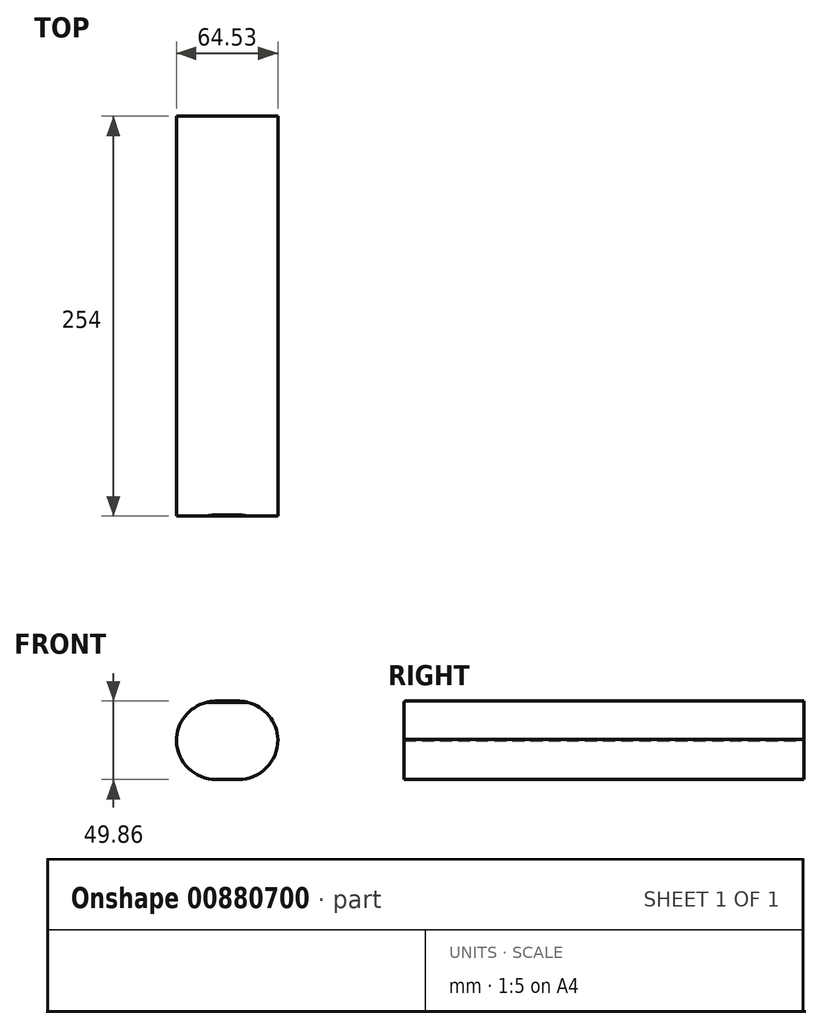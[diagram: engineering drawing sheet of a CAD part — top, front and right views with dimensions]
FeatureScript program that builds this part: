
annotation { "Feature Type Name" : "Feature", "Feature Type Description" : "" }
export const myFeature = defineFeature(function(context is Context, id is Id, definition is map)
    precondition{}
    {
        {
            var Q0;
            Q0=qCreatedBy(makeId("Front.planeOp"),FACE);
            var sketch = newSketch(context, id + "F0", { "sketchPlane" : qUnion([Q0])});
            skLineSegment(sketch, "E0.bottom", {"start": v(-64.53, 49.86) * mm, "end": v(0, 49.86) * mm});
            skLineSegment(sketch, "E0.top", {"start": v(-64.53, 0) * mm, "end": v(0, 0) * mm});
            skLineSegment(sketch, "E0.left", {"start": v(-64.53, 49.86) * mm, "end": v(-64.53, 0) * mm});
            skLineSegment(sketch, "E0.right", {"start": v(0, 49.86) * mm, "end": v(0, 0) * mm});
            skSolve(sketch);
        }
        {
            var Q0;
            Q0 = qSketchRegion(id + "F0", true);
            extrude(context, id + "F1", {"entities" : qUnion([Q0]), "depth" : 127 * mm, "offsetDistance" : 25.4 * mm, "hasSecondDirection" : true, "secondDirectionOppositeDirection" : true, "secondDirectionDepth" : 127 * mm});
        }
        {
            var Q0;
            Q0=makeQuery(id+"F1.opExtrude","CAP_FACE",FACE,{"disambiguationData":[OSD([sQuery(id+"F0.wireOp",EDGE,"E0.bottom"),sQuery(id+"F0.wireOp",EDGE,"E0.top"),sQuery(id+"F0.wireOp",EDGE,"E0.left"),sQuery(id+"F0.wireOp",EDGE,"E0.right")])],"isStart":false});
            var sketch = newSketch(context, id + "F2", { "sketchPlane" : qUnion([Q0])});
            skCircle(sketch, "E1", {"center": v(-34.08, 24.93) * mm, "radius": 15.41 * mm});
            skPoint(sketch, "E1.centerSnap0", {"position": v(-64.53, 24.93) * mm});
            skSolve(sketch);
        }
        {
            var Q0;
            Q0=makeQuery(id+"F1.opExtrude","CAP_EDGE",EDGE,{"disambiguationData":[OSD([sQuery(id+"F0.wireOp",EDGE,"E0.bottom")])],"isStart":false});
            chamfer(context, id + "F3", {"entities" : qUnion([Q0]), "width" : 0.76 * mm, "tangentPropagation" : true});
        }
        {
            var Q0;
            Q0=makeQuery(id+"F1.opExtrude","SWEPT_EDGE",EDGE,{"disambiguationData":[OSD([sQuery(id+"F0.wireOp",EDGE,"E0.bottom"),sQuery(id+"F0.wireOp",EDGE,"E0.left")])]});
            var Q1;
            {var subQ0=sQuery(id+"F0.wireOp",EDGE,"E0.right");Q1=makeQuery(id+"F9umjA94MgGjPcI_1.opFillet","BLEND_EDGE",EDGE,{"blendedFrom":[makeQuery(id+"F1.opExtrude","SWEPT_EDGE",EDGE,{"disambiguationData":[OSD([sQuery(id+"F0.wireOp",EDGE,"E0.bottom"),subQ0])]}),makeQuery(id+"F1.opExtrude","SWEPT_FACE",FACE,{"disambiguationData":[OSD([subQ0])]})],"blendedInto":[makeQuery(id+"F1.opExtrude","SWEPT_FACE",FACE,{"disambiguationData":[OSD([subQ0])]})]});}
            fillet(context, id + "F4", {"entities" : qUnion([Q0, Q1]), "radius" : 25.4 * mm, "tangentPropagation" : true, "allowEdgeOverflow" : false});
        }
        {
            var Q0;
            Q0=makeQuery(id+"F1.opExtrude","SWEPT_EDGE",EDGE,{"disambiguationData":[OSD([sQuery(id+"F0.wireOp",EDGE,"E0.top"),sQuery(id+"F0.wireOp",EDGE,"E0.left")])]});
            fillet(context, id + "F5", {"entities" : qUnion([Q0]), "radius" : 25.4 * mm, "tangentPropagation" : true, "allowEdgeOverflow" : false});
        }
        {
            var Q0;
            Q0=makeQuery(id+"F1.opExtrude","SWEPT_EDGE",EDGE,{"disambiguationData":[OSD([sQuery(id+"F0.wireOp",EDGE,"E0.top"),sQuery(id+"F0.wireOp",EDGE,"E0.right")])]});
            fillet(context, id + "F6", {"entities" : qUnion([Q0]), "radius" : 25.4 * mm, "tangentPropagation" : true, "allowEdgeOverflow" : false});
        }
        {
            var Q0;
            Q0=makeQuery(id+"F1.opExtrude","SWEPT_EDGE",EDGE,{"disambiguationData":[OSD([sQuery(id+"F0.wireOp",EDGE,"E0.bottom"),sQuery(id+"F0.wireOp",EDGE,"E0.right")])]});
            fillet(context, id + "F7", {"entities" : qUnion([Q0]), "radius" : 25.4 * mm, "tangentPropagation" : true, "allowEdgeOverflow" : false});
        }
        {
            var Q1;
            Q1=makeQuery(id+"F4.opFillet","BLEND_FACE",FACE,{"disambiguationData":[OSD([sQuery(id+"F0.wireOp",EDGE,"E0.bottom"),sQuery(id+"F0.wireOp",EDGE,"E0.left")])]});
            var Q2;
            Q2=makeQuery(id+"F7.opFillet","BLEND_FACE",FACE,{"disambiguationData":[OSD([sQuery(id+"F0.wireOp",EDGE,"E0.bottom"),sQuery(id+"F0.wireOp",EDGE,"E0.right")])]});
            loft(context, id + "F8", {"operationType" : NewBodyOperationType.ADD, "sheetProfilesArray" : [{ "sheetProfileEntities" : qUnion([Q1]) }, { "sheetProfileEntities" : qUnion([Q2]) }]});
        }
    });
